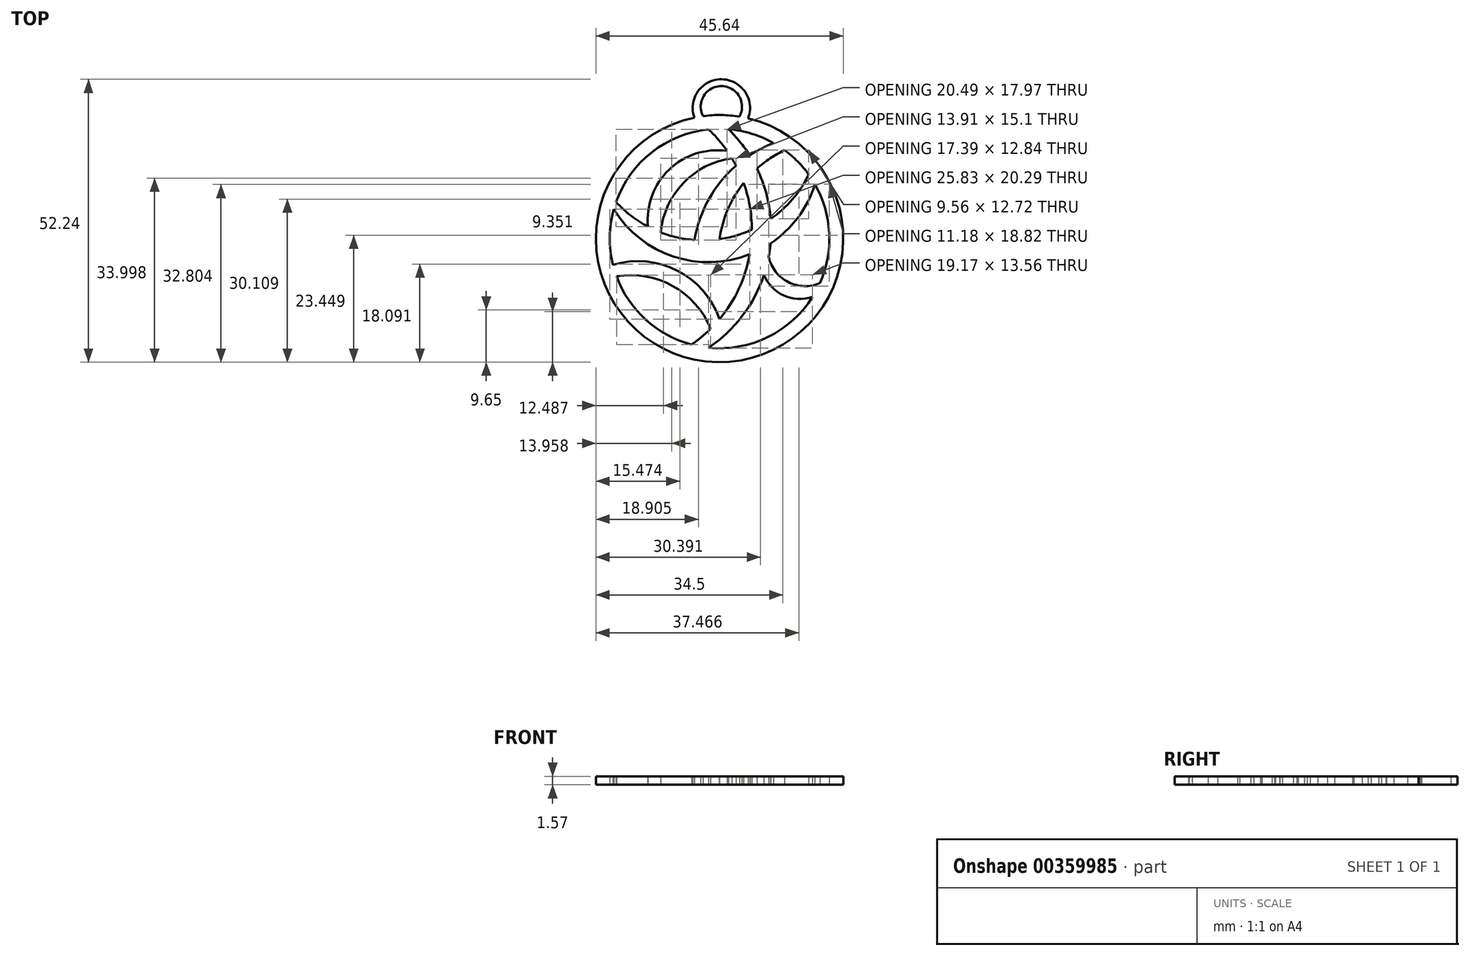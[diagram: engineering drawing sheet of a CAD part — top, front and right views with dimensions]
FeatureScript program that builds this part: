
annotation { "Feature Type Name" : "Feature", "Feature Type Description" : "" }
export const myFeature = defineFeature(function(context is Context, id is Id, definition is map)
    precondition{}
    {
        {
            var Q0;
            Q0=qCreatedBy(makeId("Top.planeOp"),FACE);
            var sketch = newSketch(context, id + "F0", { "sketchPlane" : qUnion([Q0])});
            skArc(sketch, "E0", {"start": v(-2.02, 20.16) * mm, "mid": v(-12.5, 15.94) * mm, "end": v(-19.1, 6.75) * mm});
            skArc(sketch, "E1", {"start": v(-4.66, 22.34) * mm, "mid": v(-0.3, -22.82) * mm, "end": v(5.26, 22.2) * mm});
            skArc(sketch, "E2", {"start": v(-19.52, 5.42) * mm, "mid": v(-8.5, -3.32) * mm, "end": v(5.57, -2.91) * mm});
            skArc(sketch, "E3", {"start": v(-19.1, 6.75) * mm, "mid": v(-16.35, 4.22) * mm, "end": v(-13.2, 2.2) * mm});
            skArc(sketch, "E4", {"start": v(-2.02, -20.16) * mm, "mid": v(4.2, -14.27) * mm, "end": v(8.2, -6.7) * mm});
            skArc(sketch, "E5", {"start": v(-5.18, -19.59) * mm, "mid": v(-3.35, -18.2) * mm, "end": v(-1.64, -16.66) * mm});
            skArc(sketch, "E6", {"start": v(1.38, 16.2) * mm, "mid": v(-9.31, 12.74) * mm, "end": v(-13.2, 2.2) * mm});
            skArc(sketch, "E7", {"start": v(2.26, 14.84) * mm, "mid": v(-6.68, 10.26) * mm, "end": v(-10.87, 1.14) * mm});
            skArc(sketch, "E8", {"start": v(0, -14.88) * mm, "mid": v(-7.82, -5.91) * mm, "end": v(-19.67, -4.85) * mm});
            skArc(sketch, "E9", {"start": v(-1.64, -16.66) * mm, "mid": v(-8.63, -8.77) * mm, "end": v(-19.03, -6.97) * mm});
            skArc(sketch, "E10", {"start": v(9.08, -3.43) * mm, "mid": v(12.68, -8.03) * mm, "end": v(18.52, -8.22) * mm});
            skArc(sketch, "E11", {"start": v(8.2, -6.7) * mm, "mid": v(11.86, -10.53) * mm, "end": v(17.16, -10.78) * mm});
            skArc(sketch, "E12", {"start": v(9.98, 17.63) * mm, "mid": v(7.7, 16.62) * mm, "end": v(5.55, 15.36) * mm});
            skArc(sketch, "E13", {"start": v(11.98, 16.34) * mm, "mid": v(9.32, 14.8) * mm, "end": v(6.9, 12.92) * mm});
            skArc(sketch, "E14.trimOffspring", {"start": v(5.55, 15.36) * mm, "mid": v(3.75, 17.9) * mm, "end": v(1.67, 20.2) * mm});
            skArc(sketch, "E15.trimOffspring", {"start": v(3.04, 13.46) * mm, "mid": v(2.66, 14.15) * mm, "end": v(2.26, 14.84) * mm});
            skArc(sketch, "E16.trimOffspring", {"start": v(4.44, 10.28) * mm, "mid": v(1.54, 5.43) * mm, "end": v(0, 0) * mm});
            skArc(sketch, "E17.trimOffspring", {"start": v(3.04, 13.46) * mm, "mid": v(-1.99, 7.27) * mm, "end": v(-4.64, -0.26) * mm});
            skArc(sketch, "E18.trimOffspring", {"start": v(1.38, 16.2) * mm, "mid": v(-0.22, 18.27) * mm, "end": v(-2.02, 20.16) * mm});
            skArc(sketch, "E19.trimOffspring", {"start": v(-10.87, 1.14) * mm, "mid": v(-7.8, 0.2) * mm, "end": v(-4.64, -0.26) * mm});
            skArc(sketch, "E20.trimOffspring", {"start": v(9.98, 17.63) * mm, "mid": v(5.96, 19.37) * mm, "end": v(1.67, 20.2) * mm});
            skArc(sketch, "E21.trimOffspring", {"start": v(16.46, 11.82) * mm, "mid": v(14.4, 14.26) * mm, "end": v(11.98, 16.34) * mm});
            skArc(sketch, "E22.trimOffspring", {"start": v(-19.52, 5.42) * mm, "mid": v(-20.26, 0.3) * mm, "end": v(-19.67, -4.85) * mm});
            skArc(sketch, "E23.trimOffspring", {"start": v(-19.03, -6.97) * mm, "mid": v(-13.65, -14.98) * mm, "end": v(-5.18, -19.59) * mm});
            skArc(sketch, "E24.trimOffspring", {"start": v(0, -14.88) * mm, "mid": v(3.57, -9.26) * mm, "end": v(5.57, -2.91) * mm});
            skArc(sketch, "E25.trimOffspring", {"start": v(-2.02, -20.16) * mm, "mid": v(8.9, -18.2) * mm, "end": v(17.16, -10.78) * mm});
            skArc(sketch, "E26.trimOffspring", {"start": v(18.52, -8.22) * mm, "mid": v(20.24, 1.02) * mm, "end": v(17.6, 10.04) * mm});
            skLineSegment(sketch, "E27", {"start": v(9.08, -3.43) * mm, "end": v(9.06, -3.38) * mm});
            skArc(sketch, "E28.trimOffspring", {"start": v(9.06, -3.38) * mm, "mid": v(9.26, -2.14) * mm, "end": v(9.4, -0.9) * mm});
            skArc(sketch, "E29.trimOffspring", {"start": v(9.43, 3.62) * mm, "mid": v(13.46, 7.28) * mm, "end": v(16.46, 11.82) * mm});
            skArc(sketch, "E30.trimOffspring", {"start": v(9.43, 3.62) * mm, "mid": v(8.6, 8.39) * mm, "end": v(6.9, 12.92) * mm});
            skArc(sketch, "E31.trimOffspring", {"start": v(5.96, 1.64) * mm, "mid": v(5.57, 6.03) * mm, "end": v(4.44, 10.28) * mm});
            skLineSegment(sketch, "E32", {"start": v(0, 0) * mm, "end": v(-0.06, -0.1) * mm});
            skArc(sketch, "E33.trimOffspring", {"start": v(9.4, -0.9) * mm, "mid": v(14.44, 3.87) * mm, "end": v(17.6, 10.04) * mm});
            skArc(sketch, "E34.trimOffspring", {"start": v(-0.06, -0.1) * mm, "mid": v(3.02, 0.55) * mm, "end": v(5.96, 1.64) * mm});
            skArc(sketch, "E35", {"start": v(3.67, 22.52) * mm, "mid": v(0.38, 28.17) * mm, "end": v(-3.06, 22.62) * mm});
            skArc(sketch, "E36", {"start": v(5.26, 22.2) * mm, "mid": v(0.4, 29.42) * mm, "end": v(-4.66, 22.34) * mm});
            skArc(sketch, "E37.trimOffspring", {"start": v(3.67, 22.52) * mm, "mid": v(0.31, 22.82) * mm, "end": v(-3.06, 22.62) * mm});
            skSolve(sketch);
        }
        {
            var Q0;
            Q0=makeQuery(id+"F0.imprint","IMPRINT",FACE,{"disambiguationData":[TD([[makeQuery(id+"F0.imprint","IMPRINT",EDGE,{"derivedFrom":sQuery(id+"F0.wireOp",EDGE,"E0")}),-1.0]])]});
            extrude(context, id + "F1", {"entities" : qUnion([Q0]), "depth" : 1.57 * mm});
        }
    });
